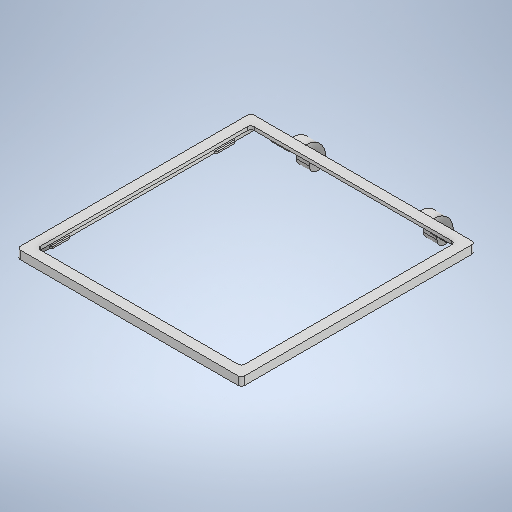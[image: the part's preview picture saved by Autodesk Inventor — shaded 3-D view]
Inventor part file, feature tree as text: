
AUTODESK INVENTOR PART (.ipt)
format: ipt  version: 2025.1 (Build 291241000, 241)  size: 432,128 bytes
history: native  units: mm
features: extrude x5, sketch x5, other x1
ambient origin geometry x8: Origin, YZ Plane, XZ Plane, XY Plane, X Axis, Y Axis, Z Axis, Center Point
bodies: Body1 (feature_tree)
feature tree (11):
  other  "Sólido1"
  extrude  "Extrusión1"  Depth=140.0mm
  extrude  "Extrusión2"  Depth=6.0mm
  extrude  "Extrusión3"  Depth=5.0mm TaperAngle=0.0deg
  extrude  "Extrusión4"  Depth=8.0mm
  extrude  "Extrusión5"  Depth=1.0mm TaperAngle=0.0deg
  sketch  "Boceto1"  dims[d0=134.4mm d1=140.0mm]
  sketch  "Boceto2"  dims[d2=2.0mm d3=6.0mm]
  sketch  "Boceto3"  dims[d4=2.0mm d5=5.0mm d6=0.0mm]
  sketch  "Boceto4"  dims[d7=25.0mm d8=8.0mm]
  sketch  "Boceto5"  dims[d9=12.0mm d10=18.0mm d11=0.0mm d13=4.25mm d14=2.75mm d16=7.0mm d17=7.0mm d18=4.0mm d19=8.0mm d20=4.0mm d21=2.0mm d25=150.0mm d26=0.0mm d27=132.0mm d28=140.0mm d29=2.5mm d30=3.0mm d31=0.0mm d32=11.0mm d33=13.0mm d36=10.0mm d37=1.0mm d38=1.0mm d40=1.0mm d41=1.0mm d42=10.0mm d43=1.0mm d44=1.0mm d45=1.0mm d46=0.0mm]
